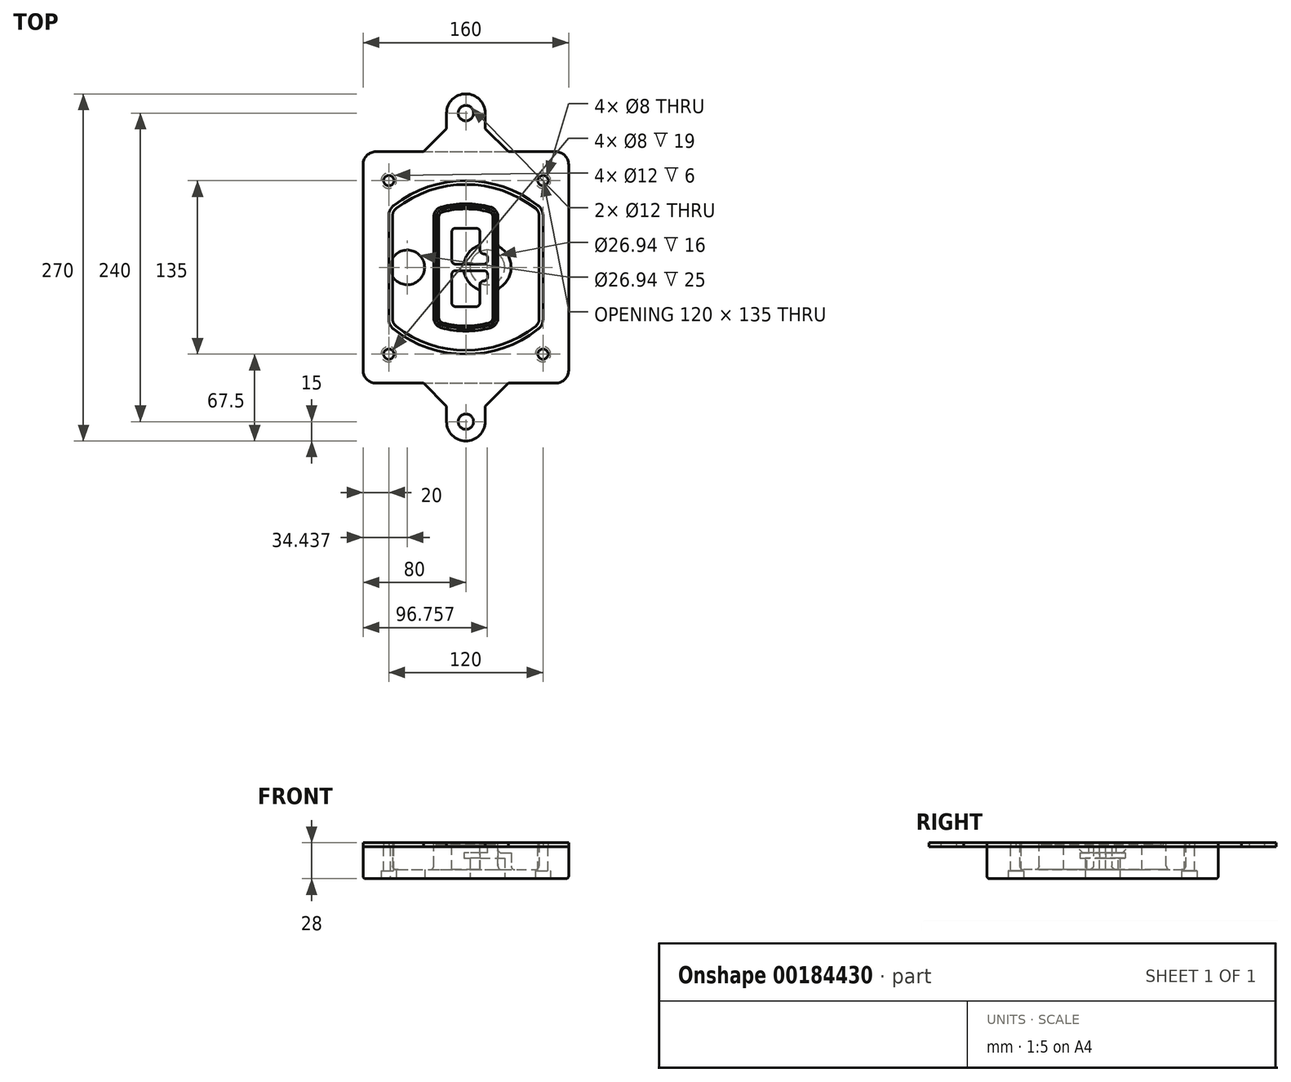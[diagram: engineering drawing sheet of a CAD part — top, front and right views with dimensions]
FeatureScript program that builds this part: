
annotation { "Feature Type Name" : "Feature", "Feature Type Description" : "" }
export const myFeature = defineFeature(function(context is Context, id is Id, definition is map)
    precondition{}
    {
        {
            var Q0;
            Q0=qCreatedBy(makeId("Top.planeOp"),FACE);
            var sketch = newSketch(context, id + "F0", { "sketchPlane" : qUnion([Q0])});
            skPoint(sketch, "E0.rect.middle", {"position": v(0, 0) * mm});
            skLineSegment(sketch, "E1.bottom", {"start": v(-70, -90) * mm, "end": v(70, -90) * mm});
            skLineSegment(sketch, "E1.top", {"start": v(-70, 90) * mm, "end": v(70, 90) * mm});
            skLineSegment(sketch, "E1.left", {"start": v(-80, -80) * mm, "end": v(-80, 80) * mm});
            skLineSegment(sketch, "E1.right", {"start": v(80, -80) * mm, "end": v(80, 80) * mm});
            skLineSegment(sketch, "E2", {"start": v(-80, 90) * mm, "end": v(80, -90) * mm, "construction": true});
            skLineSegment(sketch, "E3", {"start": v(80, 90) * mm, "end": v(-80, -90) * mm, "construction": true});
            skCircle(sketch, "E4", {"center": v(-60, 67.5) * mm, "radius": 4 * mm});
            skCircle(sketch, "E5", {"center": v(60, 67.5) * mm, "radius": 4 * mm});
            skCircle(sketch, "E6", {"center": v(60, -67.5) * mm, "radius": 4 * mm});
            skCircle(sketch, "E7", {"center": v(-60, -67.5) * mm, "radius": 4 * mm});
            skLineSegment(sketch, "E8", {"start": v(-60, 67.5) * mm, "end": v(60, 67.5) * mm, "construction": true});
            skLineSegment(sketch, "E9", {"start": v(60, 67.5) * mm, "end": v(60, -67.5) * mm, "construction": true});
            skLineSegment(sketch, "E10", {"start": v(60, -67.5) * mm, "end": v(-60, -67.5) * mm, "construction": true});
            skLineSegment(sketch, "E11", {"start": v(-60, -67.5) * mm, "end": v(-60, 67.5) * mm, "construction": true});
            skLineSegment(sketch, "E12", {"start": v(-60, 40.3) * mm, "end": v(-60, -40.3) * mm});
            skLineSegment(sketch, "E13", {"start": v(60, 40.3) * mm, "end": v(60, -40.3) * mm});
            skArc(sketch, "E14", {"start": v(56.15, 48.18) * mm, "mid": v(0, 67.5) * mm, "end": v(-56.15, 48.18) * mm});
            skArc(sketch, "E15", {"start": v(-56.15, -48.18) * mm, "mid": v(0, -67.5) * mm, "end": v(56.15, -48.18) * mm});
            skLineSegment(sketch, "E16", {"start": v(-60, 0) * mm, "end": v(60, 0) * mm, "construction": true});
            skPoint(sketch, "E17.visualSharp", {"position": v(-60, -45) * mm});
            skArc(sketch, "E17.filletArc", {"start": v(-60, -40.3) * mm, "mid": v(-58.99, -44.68) * mm, "end": v(-56.15, -48.18) * mm});
            skPoint(sketch, "E18.visualSharp", {"position": v(-60, 45) * mm});
            skArc(sketch, "E18.filletArc", {"start": v(-56.15, 48.18) * mm, "mid": v(-58.99, 44.68) * mm, "end": v(-60, 40.3) * mm});
            skPoint(sketch, "E19.visualSharp", {"position": v(60, 45) * mm});
            skArc(sketch, "E19.filletArc", {"start": v(60, 40.3) * mm, "mid": v(58.99, 44.68) * mm, "end": v(56.15, 48.18) * mm});
            skPoint(sketch, "E20.visualSharp", {"position": v(60, -45) * mm});
            skArc(sketch, "E20.filletArc", {"start": v(56.15, -48.18) * mm, "mid": v(58.99, -44.68) * mm, "end": v(60, -40.3) * mm});
            skPoint(sketch, "E21.visualSharp", {"position": v(-80, 90) * mm});
            skArc(sketch, "E21.filletArc", {"start": v(-70, 90) * mm, "mid": v(-77.07, 87.07) * mm, "end": v(-80, 80) * mm});
            skPoint(sketch, "E22.visualSharp", {"position": v(80, 90) * mm});
            skArc(sketch, "E22.filletArc", {"start": v(80, 80) * mm, "mid": v(77.07, 87.07) * mm, "end": v(70, 90) * mm});
            skPoint(sketch, "E23.visualSharp", {"position": v(80, -90) * mm});
            skArc(sketch, "E23.filletArc", {"start": v(70, -90) * mm, "mid": v(77.07, -87.07) * mm, "end": v(80, -80) * mm});
            skPoint(sketch, "E24.visualSharp", {"position": v(-80, -90) * mm});
            skArc(sketch, "E24.filletArc", {"start": v(-80, -80) * mm, "mid": v(-77.07, -87.07) * mm, "end": v(-70, -90) * mm});
            skArc(sketch, "E25.0", {"start": v(57, 40.3) * mm, "mid": v(56.3, 43.36) * mm, "end": v(54.3, 45.81) * mm});
            skLineSegment(sketch, "E25.1", {"start": v(57, 40.3) * mm, "end": v(57, -40.3) * mm});
            skArc(sketch, "E25.2", {"start": v(54.3, -45.81) * mm, "mid": v(56.3, -43.36) * mm, "end": v(57, -40.3) * mm});
            skArc(sketch, "E25.3", {"start": v(-54.3, -45.81) * mm, "mid": v(0, -64.5) * mm, "end": v(54.3, -45.81) * mm});
            skArc(sketch, "E25.4", {"start": v(-57, -40.3) * mm, "mid": v(-56.3, -43.36) * mm, "end": v(-54.3, -45.81) * mm});
            skArc(sketch, "E25.5", {"start": v(54.3, 45.81) * mm, "mid": v(0, 64.5) * mm, "end": v(-54.3, 45.81) * mm});
            skLineSegment(sketch, "E25.6", {"start": v(-57, 40.3) * mm, "end": v(-57, -40.3) * mm});
            skArc(sketch, "E25.7", {"start": v(-54.3, 45.81) * mm, "mid": v(-56.3, 43.36) * mm, "end": v(-57, 40.3) * mm});
            skArc(sketch, "E26.0", {"start": v(-58.62, 51.33) * mm, "mid": v(-62.58, 46.43) * mm, "end": v(-64, 40.3) * mm});
            skArc(sketch, "E26.1", {"start": v(58.62, 51.33) * mm, "mid": v(0, 71.5) * mm, "end": v(-58.62, 51.33) * mm});
            skArc(sketch, "E26.2", {"start": v(64, 40.3) * mm, "mid": v(62.58, 46.43) * mm, "end": v(58.62, 51.33) * mm});
            skLineSegment(sketch, "E26.3", {"start": v(64, 40.3) * mm, "end": v(64, -40.3) * mm});
            skArc(sketch, "E26.4", {"start": v(58.62, -51.33) * mm, "mid": v(62.58, -46.43) * mm, "end": v(64, -40.3) * mm});
            skLineSegment(sketch, "E26.5", {"start": v(-64, 40.3) * mm, "end": v(-64, -40.3) * mm});
            skArc(sketch, "E26.6", {"start": v(-58.62, -51.33) * mm, "mid": v(0, -71.5) * mm, "end": v(58.62, -51.33) * mm});
            skArc(sketch, "E26.7", {"start": v(-64, -40.3) * mm, "mid": v(-62.58, -46.43) * mm, "end": v(-58.62, -51.33) * mm});
            skSolve(sketch);
        }
        {
            var Q0;
            Q0=makeQuery(id+"F0.imprint","IMPRINT",FACE,{"disambiguationData":[TD([[makeQuery(id+"F0.imprint","IMPRINT",EDGE,{"derivedFrom":sQuery(id+"F0.wireOp",EDGE,"E1.bottom")}),1.0]])]});
            var Q1;
            Q1=makeQuery(id+"F0.imprint","IMPRINT",FACE,{"disambiguationData":[TD([[makeQuery(id+"F0.imprint","IMPRINT",EDGE,{"derivedFrom":sQuery(id+"F0.wireOp",EDGE,"E12")}),1.0]])]});
            var Q2;
            Q2=makeQuery(id+"F0.imprint","IMPRINT",FACE,{"disambiguationData":[TD([[makeQuery(id+"F0.imprint","IMPRINT",EDGE,{"derivedFrom":sQuery(id+"F0.wireOp",EDGE,"E25.0")}),1.0]])]});
            var Q3;
            Q3=makeQuery(id+"F0.imprint","IMPRINT",FACE,{"disambiguationData":[TD([[makeQuery(id+"F0.imprint","IMPRINT",EDGE,{"derivedFrom":sQuery(id+"F0.wireOp",EDGE,"E12")}),-1.0]])]});
            extrude(context, id + "F1", {"entities" : qUnion([Q0, Q1, Q2, Q3]), "oppositeDirection" : true, "depth" : 25 * mm});
        }
        {
            var Q0;
            Q0=makeQuery(id+"F0.imprint","IMPRINT",FACE,{"disambiguationData":[TD([[makeQuery(id+"F0.imprint","IMPRINT",EDGE,{"derivedFrom":sQuery(id+"F0.wireOp",EDGE,"E12")}),1.0]])]});
            extrude(context, id + "F2", {"entities" : qUnion([Q0]), "operationType" : NewBodyOperationType.ADD, "depth" : 3 * mm});
        }
        {
            var Q0;
            Q0=makeQuery(id+"F0.imprint","IMPRINT",FACE,{"disambiguationData":[TD([[makeQuery(id+"F0.imprint","IMPRINT",EDGE,{"derivedFrom":sQuery(id+"F0.wireOp",EDGE,"E25.0")}),1.0]])]});
            extrude(context, id + "F3", {"entities" : qUnion([Q0]), "operationType" : NewBodyOperationType.REMOVE, "oppositeDirection" : true, "depth" : 18 * mm});
        }
        {
            var Q0;
            Q0=makeQuery(id+"F2.opExtrude","CAP_FACE",FACE,{"disambiguationData":[OSD([sQuery(id+"F0.wireOp",EDGE,"E12"),sQuery(id+"F0.wireOp",EDGE,"E13"),sQuery(id+"F0.wireOp",EDGE,"E14"),sQuery(id+"F0.wireOp",EDGE,"E15"),sQuery(id+"F0.wireOp",EDGE,"E17.filletArc"),sQuery(id+"F0.wireOp",EDGE,"E18.filletArc"),sQuery(id+"F0.wireOp",EDGE,"E19.filletArc"),sQuery(id+"F0.wireOp",EDGE,"E20.filletArc"),sQuery(id+"F0.wireOp",EDGE,"E25.0"),sQuery(id+"F0.wireOp",EDGE,"E25.1"),sQuery(id+"F0.wireOp",EDGE,"E25.2"),sQuery(id+"F0.wireOp",EDGE,"E25.3"),sQuery(id+"F0.wireOp",EDGE,"E25.4"),sQuery(id+"F0.wireOp",EDGE,"E25.5"),sQuery(id+"F0.wireOp",EDGE,"E25.6"),sQuery(id+"F0.wireOp",EDGE,"E25.7")])],"isStart":false});
            var sketch = newSketch(context, id + "F4", { "sketchPlane" : qUnion([Q0])});
            skArc(sketch, "E27.0", {"start": v(-19.08, -46.97) * mm, "mid": v(0, -49.5) * mm, "end": v(19.08, -46.97) * mm});
            skArc(sketch, "E28.0", {"start": v(19.08, 46.97) * mm, "mid": v(0, 49.5) * mm, "end": v(-19.08, 46.97) * mm});
            skLineSegment(sketch, "E29", {"start": v(-25, 39.25) * mm, "end": v(-25, -39.25) * mm});
            skLineSegment(sketch, "E30", {"start": v(25, 39.25) * mm, "end": v(25, -39.25) * mm});
            skLineSegment(sketch, "E31", {"start": v(-25, 45.1) * mm, "end": v(25, 45.1) * mm, "construction": true});
            skLineSegment(sketch, "E32", {"start": v(-25, -45.1) * mm, "end": v(25, -45.1) * mm, "construction": true});
            skPoint(sketch, "E33.visualSharp", {"position": v(-25, 45.1) * mm});
            skArc(sketch, "E33.filletArc", {"start": v(-19.08, 46.97) * mm, "mid": v(-23.35, 44.11) * mm, "end": v(-25, 39.25) * mm});
            skPoint(sketch, "E34.visualSharp", {"position": v(25, 45.1) * mm});
            skArc(sketch, "E34.filletArc", {"start": v(25, 39.25) * mm, "mid": v(23.35, 44.11) * mm, "end": v(19.08, 46.97) * mm});
            skPoint(sketch, "E35.visualSharp", {"position": v(25, -45.1) * mm});
            skArc(sketch, "E35.filletArc", {"start": v(19.08, -46.97) * mm, "mid": v(23.35, -44.11) * mm, "end": v(25, -39.25) * mm});
            skPoint(sketch, "E36.visualSharp", {"position": v(-25, -45.1) * mm});
            skArc(sketch, "E36.filletArc", {"start": v(-25, -39.25) * mm, "mid": v(-23.35, -44.11) * mm, "end": v(-19.08, -46.97) * mm});
            skArc(sketch, "E37.0", {"start": v(54.3, 45.81) * mm, "mid": v(0, 64.5) * mm, "end": v(-54.3, 45.81) * mm});
            skArc(sketch, "E37.1", {"start": v(-54.3, 45.81) * mm, "mid": v(-56.3, 43.36) * mm, "end": v(-57, 40.3) * mm});
            skLineSegment(sketch, "E37.2", {"start": v(-57, 40.3) * mm, "end": v(-57, -40.3) * mm});
            skArc(sketch, "E37.3", {"start": v(-57, -40.3) * mm, "mid": v(-56.3, -43.36) * mm, "end": v(-54.3, -45.81) * mm});
            skArc(sketch, "E37.4", {"start": v(-54.3, -45.81) * mm, "mid": v(0, -64.5) * mm, "end": v(54.3, -45.81) * mm});
            skArc(sketch, "E37.5", {"start": v(54.3, -45.81) * mm, "mid": v(56.3, -43.36) * mm, "end": v(57, -40.3) * mm});
            skLineSegment(sketch, "E37.6", {"start": v(57, 40.3) * mm, "end": v(57, -40.3) * mm});
            skArc(sketch, "E37.7", {"start": v(57, 40.3) * mm, "mid": v(56.3, 43.36) * mm, "end": v(54.3, 45.81) * mm});
            skLineSegment(sketch, "E38.0", {"start": v(23, 39.25) * mm, "end": v(23, -39.25) * mm});
            skArc(sketch, "E38.1", {"start": v(18.56, -45.04) * mm, "mid": v(21.76, -42.9) * mm, "end": v(23, -39.25) * mm});
            skArc(sketch, "E38.2", {"start": v(-18.56, -45.04) * mm, "mid": v(0, -47.5) * mm, "end": v(18.56, -45.04) * mm});
            skArc(sketch, "E38.3", {"start": v(-23, -39.25) * mm, "mid": v(-21.76, -42.9) * mm, "end": v(-18.56, -45.04) * mm});
            skLineSegment(sketch, "E38.4", {"start": v(-23, 39.25) * mm, "end": v(-23, -39.25) * mm});
            skArc(sketch, "E38.5", {"start": v(23, 39.25) * mm, "mid": v(21.76, 42.9) * mm, "end": v(18.56, 45.04) * mm});
            skArc(sketch, "E38.6", {"start": v(-18.56, 45.04) * mm, "mid": v(-21.76, 42.9) * mm, "end": v(-23, 39.25) * mm});
            skArc(sketch, "E38.7", {"start": v(18.56, 45.04) * mm, "mid": v(0, 47.5) * mm, "end": v(-18.56, 45.04) * mm});
            skArc(sketch, "E39.0", {"start": v(21, 39.25) * mm, "mid": v(20.18, 41.68) * mm, "end": v(18.04, 43.1) * mm});
            skLineSegment(sketch, "E39.1", {"start": v(21, 39.25) * mm, "end": v(21, -39.25) * mm});
            skArc(sketch, "E39.2", {"start": v(18.04, -43.1) * mm, "mid": v(20.18, -41.68) * mm, "end": v(21, -39.25) * mm});
            skArc(sketch, "E39.3", {"start": v(-18.04, -43.1) * mm, "mid": v(0, -45.5) * mm, "end": v(18.04, -43.1) * mm});
            skArc(sketch, "E39.4", {"start": v(-21, -39.25) * mm, "mid": v(-20.18, -41.68) * mm, "end": v(-18.04, -43.1) * mm});
            skArc(sketch, "E39.5", {"start": v(18.04, 43.1) * mm, "mid": v(0, 45.5) * mm, "end": v(-18.04, 43.1) * mm});
            skLineSegment(sketch, "E39.6", {"start": v(-21, 39.25) * mm, "end": v(-21, -39.25) * mm});
            skArc(sketch, "E39.7", {"start": v(-18.04, 43.1) * mm, "mid": v(-20.18, 41.68) * mm, "end": v(-21, 39.25) * mm});
            skLineSegment(sketch, "E40", {"start": v(-25, 0) * mm, "end": v(25, 0) * mm, "construction": true});
            skLineSegment(sketch, "E41", {"start": v(-11, 5.5) * mm, "end": v(-11, 27.5) * mm});
            skLineSegment(sketch, "E42", {"start": v(-8, 30.5) * mm, "end": v(8, 30.5) * mm});
            skLineSegment(sketch, "E43", {"start": v(11, 27.5) * mm, "end": v(11, 13.5) * mm});
            skLineSegment(sketch, "E44", {"start": v(14, 10.5) * mm, "end": v(14, 10.5) * mm});
            skLineSegment(sketch, "E45", {"start": v(17, 7.5) * mm, "end": v(17, 5.5) * mm});
            skLineSegment(sketch, "E46", {"start": v(14, 2.5) * mm, "end": v(-8, 2.5) * mm});
            skPoint(sketch, "E47.visualSharp", {"position": v(-11, 30.5) * mm});
            skArc(sketch, "E47.filletArc", {"start": v(-8, 30.5) * mm, "mid": v(-10.12, 29.62) * mm, "end": v(-11, 27.5) * mm});
            skPoint(sketch, "E48.visualSharp", {"position": v(11, 30.5) * mm});
            skArc(sketch, "E48.filletArc", {"start": v(11, 27.5) * mm, "mid": v(10.12, 29.62) * mm, "end": v(8, 30.5) * mm});
            skPoint(sketch, "E49.visualSharp", {"position": v(11, 10.5) * mm});
            skArc(sketch, "E49.filletArc", {"start": v(11, 13.5) * mm, "mid": v(11.88, 11.38) * mm, "end": v(14, 10.5) * mm});
            skPoint(sketch, "E50.visualSharp", {"position": v(17, 10.5) * mm});
            skArc(sketch, "E50.filletArc", {"start": v(17, 7.5) * mm, "mid": v(16.12, 9.62) * mm, "end": v(14, 10.5) * mm});
            skPoint(sketch, "E51.visualSharp", {"position": v(17, 2.5) * mm});
            skArc(sketch, "E51.filletArc", {"start": v(14, 2.5) * mm, "mid": v(16.12, 3.38) * mm, "end": v(17, 5.5) * mm});
            skPoint(sketch, "E52.visualSharp", {"position": v(-11, 2.5) * mm});
            skArc(sketch, "E52.filletArc", {"start": v(-11, 5.5) * mm, "mid": v(-10.12, 3.38) * mm, "end": v(-8, 2.5) * mm});
            skLineSegment(sketch, "E53.0.MirrorCS", {"start": v(14, -2.5) * mm, "end": v(-8, -2.5) * mm});
            skArc(sketch, "E54.0.MirrorCS", {"start": v(-11, -5.5) * mm, "mid": v(-10.12, -3.38) * mm, "end": v(-8, -2.5) * mm});
            skLineSegment(sketch, "E55.0.MirrorCS", {"start": v(-11, -5.5) * mm, "end": v(-11, -27.5) * mm});
            skArc(sketch, "E56.0.MirrorCS", {"start": v(-8, -30.5) * mm, "mid": v(-10.12, -29.62) * mm, "end": v(-11, -27.5) * mm});
            skLineSegment(sketch, "E57.0.MirrorCS", {"start": v(-8, -30.5) * mm, "end": v(8, -30.5) * mm});
            skArc(sketch, "E58.0.MirrorCS", {"start": v(11, -27.5) * mm, "mid": v(10.12, -29.62) * mm, "end": v(8, -30.5) * mm});
            skLineSegment(sketch, "E59.0.MirrorCS", {"start": v(11, -27.5) * mm, "end": v(11, -13.5) * mm});
            skArc(sketch, "E60.0.MirrorCS", {"start": v(11, -13.5) * mm, "mid": v(11.88, -11.38) * mm, "end": v(14, -10.5) * mm});
            skArc(sketch, "E61.0.MirrorCS", {"start": v(17, -7.5) * mm, "mid": v(16.12, -9.62) * mm, "end": v(14, -10.5) * mm});
            skLineSegment(sketch, "E62.0.MirrorCS", {"start": v(17, -7.5) * mm, "end": v(17, -5.5) * mm});
            skArc(sketch, "E63.0.MirrorCS", {"start": v(14, -2.5) * mm, "mid": v(16.12, -3.38) * mm, "end": v(17, -5.5) * mm});
            skSolve(sketch);
        }
        {
            var Q0;
            Q0=makeQuery(id+"F4.imprint","IMPRINT",FACE,{"disambiguationData":[TD([[makeQuery(id+"F4.imprint","IMPRINT",EDGE,{"derivedFrom":sQuery(id+"F4.wireOp",EDGE,"E27.0")}),1.0]])]});
            var Q1;
            Q1=makeQuery(id+"F4.imprint","IMPRINT",FACE,{"disambiguationData":[TD([[makeQuery(id+"F4.imprint","IMPRINT",EDGE,{"derivedFrom":sQuery(id+"F4.wireOp",EDGE,"E38.0")}),-1.0]])]});
            var Q2;
            Q2=makeQuery(id+"F4.imprint","IMPRINT",FACE,{"disambiguationData":[TD([[makeQuery(id+"F4.imprint","IMPRINT",EDGE,{"derivedFrom":sQuery(id+"F4.wireOp",EDGE,"E39.0")}),1.0]])]});
            extrude(context, id + "F5", {"entities" : qUnion([Q0, Q1, Q2]), "operationType" : NewBodyOperationType.ADD, "endBound" : BoundingType.UP_TO_NEXT, "oppositeDirection" : true, "depth" : 25 * mm});
        }
        {
            var Q0;
            Q0=makeQuery(id+"F4.imprint","IMPRINT",FACE,{"disambiguationData":[TD([[makeQuery(id+"F4.imprint","IMPRINT",EDGE,{"derivedFrom":sQuery(id+"F4.wireOp",EDGE,"E38.0")}),-1.0]])]});
            extrude(context, id + "F6", {"entities" : qUnion([Q0]), "operationType" : NewBodyOperationType.REMOVE, "oppositeDirection" : true, "depth" : 2 * mm});
        }
        {
            var Q0;
            Q0=makeQuery(id+"F1.opExtrude","CAP_FACE",FACE,{"disambiguationData":[OSD([sQuery(id+"F0.wireOp",EDGE,"E1.bottom"),sQuery(id+"F0.wireOp",EDGE,"E1.top"),sQuery(id+"F0.wireOp",EDGE,"E1.left"),sQuery(id+"F0.wireOp",EDGE,"E1.right"),sQuery(id+"F0.wireOp",EDGE,"E4"),sQuery(id+"F0.wireOp",EDGE,"E5"),sQuery(id+"F0.wireOp",EDGE,"E6"),sQuery(id+"F0.wireOp",EDGE,"E7"),sQuery(id+"F0.wireOp",EDGE,"E21.filletArc"),sQuery(id+"F0.wireOp",EDGE,"E22.filletArc"),sQuery(id+"F0.wireOp",EDGE,"E23.filletArc"),sQuery(id+"F0.wireOp",EDGE,"E24.filletArc")])],"isStart":false});
            var sketch = newSketch(context, id + "F7", { "sketchPlane" : qUnion([Q0])});
            skCircle(sketch, "E64", {"center": v(16.76, 0) * mm, "radius": 13.47 * mm});
            skCircle(sketch, "E65", {"center": v(-45.56, 0) * mm, "radius": 13.47 * mm});
            skLineSegment(sketch, "E66", {"start": v(80, 0) * mm, "end": v(-80, 0) * mm});
            skCircle(sketch, "E67", {"center": v(16.76, 0) * mm, "radius": 18.47 * mm});
            skCircle(sketch, "E68", {"center": v(60, -67.5) * mm, "radius": 6 * mm});
            skCircle(sketch, "E69", {"center": v(-60, -67.5) * mm, "radius": 6 * mm});
            skCircle(sketch, "E70", {"center": v(-60, 67.5) * mm, "radius": 6 * mm});
            skCircle(sketch, "E71", {"center": v(60, 67.5) * mm, "radius": 6 * mm});
            skSolve(sketch);
        }
        {
            var Q0;
            {var subQ1=sQuery(id+"F7.wireOp",EDGE,"E66");var subQ4=sQuery(id+"F7.wireOp",EDGE,"E64");var subQ6=makeQuery(id+"F7.imprint","INTERSECT",VERTEX,{"disambiguationData":[OD(0.0)],"derivedFrom":[subQ4,subQ1]});Q0=makeQuery(id+"F7.imprint","IMPRINT",FACE,{"disambiguationData":[TD([[makeQuery(id+"F7.imprint","IMPRINT",EDGE,{"disambiguationData":[TD([[subQ6,-1.0]])],"derivedFrom":subQ4}),-1.0]])]});}
            var Q1;
            {var subQ0=sQuery(id+"F7.wireOp",EDGE,"E66");var subQ1=sQuery(id+"F7.wireOp",EDGE,"E64");var subQ3=makeQuery(id+"F7.imprint","INTERSECT",VERTEX,{"disambiguationData":[OD(0.0)],"derivedFrom":[subQ1,subQ0]});Q1=makeQuery(id+"F7.imprint","IMPRINT",FACE,{"disambiguationData":[TD([[makeQuery(id+"F7.imprint","IMPRINT",EDGE,{"disambiguationData":[TD([[subQ3,-1.0]])],"derivedFrom":subQ1}),1.0]])]});}
            var Q2;
            {var subQ0=sQuery(id+"F7.wireOp",EDGE,"E66");var subQ1=sQuery(id+"F7.wireOp",EDGE,"E64");var subQ3=makeQuery(id+"F7.imprint","INTERSECT",VERTEX,{"disambiguationData":[OD(0.0)],"derivedFrom":[subQ1,subQ0]});Q2=makeQuery(id+"F7.imprint","IMPRINT",FACE,{"disambiguationData":[TD([[makeQuery(id+"F7.imprint","IMPRINT",EDGE,{"disambiguationData":[TD([[subQ3,1.0]])],"derivedFrom":subQ1}),1.0]])]});}
            var Q3;
            {var subQ1=sQuery(id+"F7.wireOp",EDGE,"E66");var subQ4=sQuery(id+"F7.wireOp",EDGE,"E64");var subQ6=makeQuery(id+"F7.imprint","INTERSECT",VERTEX,{"disambiguationData":[OD(0.0)],"derivedFrom":[subQ4,subQ1]});Q3=makeQuery(id+"F7.imprint","IMPRINT",FACE,{"disambiguationData":[TD([[makeQuery(id+"F7.imprint","IMPRINT",EDGE,{"disambiguationData":[TD([[subQ6,1.0]])],"derivedFrom":subQ4}),-1.0]])]});}
            extrude(context, id + "F8", {"entities" : qUnion([Q0, Q1, Q2, Q3]), "operationType" : NewBodyOperationType.ADD, "oppositeDirection" : true, "depth" : 20 * mm});
        }
        {
            var Q0;
            {var subQ0=sQuery(id+"F7.wireOp",EDGE,"E66");var subQ1=sQuery(id+"F7.wireOp",EDGE,"E64");var subQ3=makeQuery(id+"F7.imprint","INTERSECT",VERTEX,{"disambiguationData":[OD(0.0)],"derivedFrom":[subQ1,subQ0]});Q0=makeQuery(id+"F7.imprint","IMPRINT",FACE,{"disambiguationData":[TD([[makeQuery(id+"F7.imprint","IMPRINT",EDGE,{"disambiguationData":[TD([[subQ3,-1.0]])],"derivedFrom":subQ1}),1.0]])]});}
            var Q1;
            {var subQ0=sQuery(id+"F7.wireOp",EDGE,"E66");var subQ1=sQuery(id+"F7.wireOp",EDGE,"E64");var subQ3=makeQuery(id+"F7.imprint","INTERSECT",VERTEX,{"disambiguationData":[OD(0.0)],"derivedFrom":[subQ1,subQ0]});Q1=makeQuery(id+"F7.imprint","IMPRINT",FACE,{"disambiguationData":[TD([[makeQuery(id+"F7.imprint","IMPRINT",EDGE,{"disambiguationData":[TD([[subQ3,1.0]])],"derivedFrom":subQ1}),1.0]])]});}
            extrude(context, id + "F9", {"entities" : qUnion([Q0, Q1]), "operationType" : NewBodyOperationType.REMOVE, "oppositeDirection" : true, "depth" : 16 * mm});
        }
        {
            var Q0;
            {var subQ0=sQuery(id+"F7.wireOp",EDGE,"E66");var subQ1=sQuery(id+"F7.wireOp",EDGE,"E65");var subQ3=makeQuery(id+"F7.imprint","INTERSECT",VERTEX,{"disambiguationData":[OD(0.0)],"derivedFrom":[subQ1,subQ0]});Q0=makeQuery(id+"F7.imprint","IMPRINT",FACE,{"disambiguationData":[TD([[makeQuery(id+"F7.imprint","IMPRINT",EDGE,{"disambiguationData":[TD([[subQ3,-1.0]])],"derivedFrom":subQ1}),1.0]])]});}
            var Q1;
            {var subQ0=sQuery(id+"F7.wireOp",EDGE,"E66");var subQ1=sQuery(id+"F7.wireOp",EDGE,"E65");var subQ3=makeQuery(id+"F7.imprint","INTERSECT",VERTEX,{"disambiguationData":[OD(0.0)],"derivedFrom":[subQ1,subQ0]});Q1=makeQuery(id+"F7.imprint","IMPRINT",FACE,{"disambiguationData":[TD([[makeQuery(id+"F7.imprint","IMPRINT",EDGE,{"disambiguationData":[TD([[subQ3,1.0]])],"derivedFrom":subQ1}),1.0]])]});}
            extrude(context, id + "F10", {"entities" : qUnion([Q0, Q1]), "operationType" : NewBodyOperationType.REMOVE, "oppositeDirection" : true, "depth" : 25 * mm});
        }
        {
            var Q0;
            Q0=makeQuery(id+"F7.imprint","IMPRINT",FACE,{"disambiguationData":[TD([[makeQuery(id+"F7.imprint","IMPRINT",EDGE,{"derivedFrom":sQuery(id+"F7.wireOp",EDGE,"E68")}),1.0]])]});
            var Q1;
            Q1=makeQuery(id+"F7.imprint","IMPRINT",FACE,{"disambiguationData":[TD([[makeQuery(id+"F7.imprint","IMPRINT",EDGE,{"derivedFrom":makeQuery(id+"F1.opExtrude","CAP_EDGE",EDGE,{"disambiguationData":[OSD([sQuery(id+"F0.wireOp",EDGE,"E5")])],"isStart":false})}),-1.0]])]});
            var Q2;
            Q2=makeQuery(id+"F7.imprint","IMPRINT",FACE,{"disambiguationData":[TD([[makeQuery(id+"F7.imprint","IMPRINT",EDGE,{"derivedFrom":sQuery(id+"F7.wireOp",EDGE,"E69")}),1.0]])]});
            var Q3;
            Q3=makeQuery(id+"F7.imprint","IMPRINT",FACE,{"disambiguationData":[TD([[makeQuery(id+"F7.imprint","IMPRINT",EDGE,{"derivedFrom":makeQuery(id+"F1.opExtrude","CAP_EDGE",EDGE,{"disambiguationData":[OSD([sQuery(id+"F0.wireOp",EDGE,"E4")])],"isStart":false})}),-1.0]])]});
            var Q4;
            Q4=makeQuery(id+"F7.imprint","IMPRINT",FACE,{"disambiguationData":[TD([[makeQuery(id+"F7.imprint","IMPRINT",EDGE,{"derivedFrom":sQuery(id+"F7.wireOp",EDGE,"E70")}),1.0]])]});
            var Q5;
            Q5=makeQuery(id+"F7.imprint","IMPRINT",FACE,{"disambiguationData":[TD([[makeQuery(id+"F7.imprint","IMPRINT",EDGE,{"derivedFrom":makeQuery(id+"F1.opExtrude","CAP_EDGE",EDGE,{"disambiguationData":[OSD([sQuery(id+"F0.wireOp",EDGE,"E7")])],"isStart":false})}),-1.0]])]});
            var Q6;
            Q6=makeQuery(id+"F7.imprint","IMPRINT",FACE,{"disambiguationData":[TD([[makeQuery(id+"F7.imprint","IMPRINT",EDGE,{"derivedFrom":sQuery(id+"F7.wireOp",EDGE,"E71")}),1.0]])]});
            var Q7;
            Q7=makeQuery(id+"F7.imprint","IMPRINT",FACE,{"disambiguationData":[TD([[makeQuery(id+"F7.imprint","IMPRINT",EDGE,{"derivedFrom":makeQuery(id+"F1.opExtrude","CAP_EDGE",EDGE,{"disambiguationData":[OSD([sQuery(id+"F0.wireOp",EDGE,"E6")])],"isStart":false})}),-1.0]])]});
            extrude(context, id + "F11", {"entities" : qUnion([Q0, Q1, Q2, Q3, Q4, Q5, Q6, Q7]), "operationType" : NewBodyOperationType.REMOVE, "oppositeDirection" : true, "depth" : 6 * mm});
        }
        {
            var Q0;
            Q0=makeQuery(id+"F9.boolean.opBoolean","COPY",FACE,{"derivedFrom":makeQuery(id+"F9.opExtrude","CAP_FACE",FACE,{"disambiguationData":[OSD([sQuery(id+"F7.wireOp",EDGE,"E64")])],"isStart":false})});
            var sketch = newSketch(context, id + "F12", { "sketchPlane" : qUnion([Q0])});
            skArc(sketch, "E72.0", {"start": v(11, 17.55) * mm, "mid": v(2.57, 11.82) * mm, "end": v(-1.54, 2.5) * mm});
            skArc(sketch, "E72.1", {"start": v(-1.54, -2.5) * mm, "mid": v(2.57, -11.82) * mm, "end": v(11, -17.55) * mm});
            skLineSegment(sketch, "E73", {"start": v(-1.54, -2.5) * mm, "end": v(14, -2.5) * mm});
            skLineSegment(sketch, "E74.0", {"start": v(14, 2.5) * mm, "end": v(-1.54, 2.5) * mm});
            skArc(sketch, "E74.1", {"start": v(14, 2.5) * mm, "mid": v(16.12, 3.38) * mm, "end": v(17, 5.5) * mm});
            skLineSegment(sketch, "E74.2", {"start": v(17, 7.5) * mm, "end": v(17, 5.5) * mm});
            skArc(sketch, "E74.3", {"start": v(17, 7.5) * mm, "mid": v(16.12, 9.62) * mm, "end": v(14, 10.5) * mm});
            skArc(sketch, "E74.4", {"start": v(11, 13.5) * mm, "mid": v(11.88, 11.38) * mm, "end": v(14, 10.5) * mm});
            skLineSegment(sketch, "E74.5", {"start": v(11, 17.55) * mm, "end": v(11, 13.5) * mm});
            skLineSegment(sketch, "E74.7", {"start": v(14, -2.5) * mm, "end": v(-1.54, -2.5) * mm});
            skArc(sketch, "E74.8", {"start": v(14, -2.5) * mm, "mid": v(16.12, -3.38) * mm, "end": v(17, -5.5) * mm});
            skLineSegment(sketch, "E74.9", {"start": v(17, -7.5) * mm, "end": v(17, -5.5) * mm});
            skArc(sketch, "E74.10", {"start": v(17, -7.5) * mm, "mid": v(16.12, -9.62) * mm, "end": v(14, -10.5) * mm});
            skArc(sketch, "E74.11", {"start": v(11, -13.5) * mm, "mid": v(11.88, -11.38) * mm, "end": v(14, -10.5) * mm});
            skLineSegment(sketch, "E74.12", {"start": v(11, -17.55) * mm, "end": v(11, -13.5) * mm});
            skPoint(sketch, "E75.orphan", {"position": v(11, -27.5) * mm});
            skPoint(sketch, "E76.orphan", {"position": v(-8, -2.5) * mm});
            skPoint(sketch, "E77.orphan", {"position": v(-8, 2.5) * mm});
            skPoint(sketch, "E78.orphan", {"position": v(11, 27.5) * mm});
            skSolve(sketch);
        }
        {
            var Q0;
            {var subQ7=sQuery(id+"F12.wireOp",EDGE,"E72.0");var subQ14=sQuery(id+"F12.wireOp",EDGE,"E72.1");var subQ16=sQuery(id+"F12.wireOp",EDGE,"E74.1");var subQ18=sQuery(id+"F12.wireOp",EDGE,"E74.8");Q0=qUnion([makeQuery(id+"F12.imprint","IMPRINT",FACE,{"disambiguationData":[TD([[makeQuery(id+"F12.imprint","IMPRINT",EDGE,{"derivedFrom":subQ7}),1.0]])]}),makeQuery(id+"F12.imprint","IMPRINT",FACE,{"disambiguationData":[TD([[makeQuery(id+"F12.imprint","IMPRINT",EDGE,{"derivedFrom":subQ14}),1.0]])]}),makeQuery(id+"F12.imprint","IMPRINT",FACE,{"disambiguationData":[TD([[makeQuery(id+"F12.imprint","IMPRINT",EDGE,{"derivedFrom":subQ16}),1.0]])]}),makeQuery(id+"F12.imprint","IMPRINT",FACE,{"disambiguationData":[TD([[makeQuery(id+"F12.imprint","IMPRINT",EDGE,{"derivedFrom":subQ18}),-1.0]])]})]);}
            var Q1;
            Q1=makeQuery(id+"F5.boolean.opBoolean","SPLIT",FACE,{"disambiguationData":[TD([makeQuery(id+"F5.opExtrude","SWEPT_FACE",FACE,{"disambiguationData":[OSD([sQuery(id+"F4.wireOp",EDGE,"E41")])]})])],"derivedFrom":makeQuery(id+"F3.boolean.opBoolean","COPY",FACE,{"derivedFrom":makeQuery(id+"F3.opExtrude","CAP_FACE",FACE,{"disambiguationData":[OSD([sQuery(id+"F0.wireOp",EDGE,"E25.0"),sQuery(id+"F0.wireOp",EDGE,"E25.1"),sQuery(id+"F0.wireOp",EDGE,"E25.2"),sQuery(id+"F0.wireOp",EDGE,"E25.3"),sQuery(id+"F0.wireOp",EDGE,"E25.4"),sQuery(id+"F0.wireOp",EDGE,"E25.5"),sQuery(id+"F0.wireOp",EDGE,"E25.6"),sQuery(id+"F0.wireOp",EDGE,"E25.7")])],"isStart":false})})});
            extrude(context, id + "F13", {"entities" : qUnion([Q0]), "operationType" : NewBodyOperationType.REMOVE, "endBound" : BoundingType.UP_TO_SURFACE, "endBoundEntityFace" : qUnion([Q1]), "depth" : 25 * mm});
        }
        {
            var Q0;
            Q0=makeQuery(id+"F3.boolean.opBoolean","COPY",EDGE,{"derivedFrom":makeQuery(id+"F3.opExtrude","CAP_EDGE",EDGE,{"disambiguationData":[OSD([sQuery(id+"F0.wireOp",EDGE,"E25.6")])],"isStart":false})});
            var Q1;
            Q1=makeQuery(id+"F8.boolean.opBoolean","INTERSECT",EDGE,{"derivedFrom":[makeQuery(id+"F5.opExtrude","SWEPT_FACE",FACE,{"disambiguationData":[OSD([sQuery(id+"F4.wireOp",EDGE,"E30")])]}),makeQuery(id+"F8.opExtrude","CAP_FACE",FACE,{"disambiguationData":[OSD([sQuery(id+"F7.wireOp",EDGE,"E67")])],"isStart":false})]});
            var Q2;
            Q2=makeQuery(id+"F8.boolean.opBoolean","INTERSECT",EDGE,{"disambiguationData":[OD(1.0)],"derivedFrom":[makeQuery(id+"F5.opExtrude","SWEPT_FACE",FACE,{"disambiguationData":[OSD([sQuery(id+"F4.wireOp",EDGE,"E30")])]}),makeQuery(id+"F8.opExtrude","SWEPT_FACE",FACE,{"disambiguationData":[OSD([sQuery(id+"F7.wireOp",EDGE,"E67")])]})]});
            var Q3;
            {var subQ0=sQuery(id+"F4.wireOp",EDGE,"E30");Q3=makeQuery(id+"F8.boolean.opBoolean","SPLIT",EDGE,{"disambiguationData":[TD([makeQuery(id+"F5.opExtrude","SWEPT_FACE",FACE,{"disambiguationData":[OSD([sQuery(id+"F4.wireOp",EDGE,"E35.filletArc")])]})])],"derivedFrom":makeQuery(id+"F5.opExtrude","CAP_EDGE",EDGE,{"disambiguationData":[OSD([subQ0])],"isStart":false})});}
            var Q4;
            {var subQ0=sQuery(id+"F0.wireOp",EDGE,"E25.7");var subQ1=sQuery(id+"F0.wireOp",EDGE,"E25.1");var subQ2=sQuery(id+"F0.wireOp",EDGE,"E25.6");var subQ3=sQuery(id+"F0.wireOp",EDGE,"E25.5");var subQ4=sQuery(id+"F0.wireOp",EDGE,"E25.4");var subQ5=sQuery(id+"F0.wireOp",EDGE,"E25.0");var subQ6=sQuery(id+"F0.wireOp",EDGE,"E25.2");var subQ7=sQuery(id+"F0.wireOp",EDGE,"E25.3");Q4=makeQuery(id+"F8.boolean.opBoolean","INTERSECT",EDGE,{"derivedFrom":[makeQuery(id+"F5.boolean.opBoolean","SPLIT",FACE,{"disambiguationData":[TD([makeQuery(id+"F2.opExtrude","SWEPT_FACE",FACE,{"disambiguationData":[OSD([subQ5])]})])],"derivedFrom":makeQuery(id+"F3.boolean.opBoolean","COPY",FACE,{"derivedFrom":makeQuery(id+"F3.opExtrude","CAP_FACE",FACE,{"disambiguationData":[OSD([subQ5,subQ1,subQ6,subQ7,subQ4,subQ3,subQ2,subQ0])],"isStart":false})})}),makeQuery(id+"F8.opExtrude","SWEPT_FACE",FACE,{"disambiguationData":[OSD([sQuery(id+"F7.wireOp",EDGE,"E67")])]})]});}
            var Q5;
            Q5=makeQuery(id+"F8.boolean.opBoolean","INTERSECT",EDGE,{"disambiguationData":[OD(0.0)],"derivedFrom":[makeQuery(id+"F5.opExtrude","SWEPT_FACE",FACE,{"disambiguationData":[OSD([sQuery(id+"F4.wireOp",EDGE,"E30")])]}),makeQuery(id+"F8.opExtrude","SWEPT_FACE",FACE,{"disambiguationData":[OSD([sQuery(id+"F7.wireOp",EDGE,"E67")])]})]});
            fillet(context, id + "F14", {"entities" : qUnion([Q0, Q1, Q2, Q3, Q4, Q5]), "radius" : 3 * mm, "tangentPropagation" : true, "allowEdgeOverflow" : false});
        }
        {
            var Q0;
            Q0=makeQuery(id+"F1.opExtrude","CAP_EDGE",EDGE,{"disambiguationData":[OSD([sQuery(id+"F0.wireOp",EDGE,"E1.bottom")])],"isStart":false});
            fillet(context, id + "F15", {"entities" : qUnion([Q0]), "radius" : 2 * mm, "tangentPropagation" : true, "allowEdgeOverflow" : false});
        }
        {
            var Q0;
            {var subQ0=sQuery(id+"F0.wireOp",EDGE,"E22.filletArc");var subQ1=sQuery(id+"F0.wireOp",EDGE,"E7");var subQ2=sQuery(id+"F0.wireOp",EDGE,"E6");var subQ3=sQuery(id+"F0.wireOp",EDGE,"E5");var subQ4=sQuery(id+"F0.wireOp",EDGE,"E4");var subQ5=sQuery(id+"F0.wireOp",EDGE,"E1.bottom");var subQ6=sQuery(id+"F0.wireOp",EDGE,"E21.filletArc");var subQ7=sQuery(id+"F0.wireOp",EDGE,"E1.top");var subQ8=sQuery(id+"F0.wireOp",EDGE,"E1.left");var subQ9=sQuery(id+"F0.wireOp",EDGE,"E1.right");var subQ10=sQuery(id+"F0.wireOp",EDGE,"E23.filletArc");var subQ11=sQuery(id+"F0.wireOp",EDGE,"E24.filletArc");Q0=makeQuery(id+"F2.boolean.opBoolean","SPLIT",FACE,{"disambiguationData":[TD([makeQuery(id+"F1.opExtrude","SWEPT_FACE",FACE,{"disambiguationData":[OSD([subQ5])]})])],"derivedFrom":makeQuery(id+"F1.opExtrude","CAP_FACE",FACE,{"disambiguationData":[OSD([subQ5,subQ7,subQ8,subQ9,subQ4,subQ3,subQ2,subQ1,subQ6,subQ0,subQ10,subQ11])],"isStart":true})});}
            var sketch = newSketch(context, id + "F16", { "sketchPlane" : qUnion([Q0])});
            skLineSegment(sketch, "E79", {"start": v(0, 90) * mm, "end": v(0, 120) * mm, "construction": true});
            skCircle(sketch, "E80", {"center": v(0, 120) * mm, "radius": 6 * mm});
            skLineSegment(sketch, "E81", {"start": v(15, 120) * mm, "end": v(15, 108) * mm});
            skLineSegment(sketch, "E82", {"start": v(15, 108) * mm, "end": v(33, 90) * mm});
            skArc(sketch, "E83", {"start": v(15, 120) * mm, "mid": v(0, 135) * mm, "end": v(-15, 120) * mm});
            skLineSegment(sketch, "E84", {"start": v(-15, 120) * mm, "end": v(-15, 108) * mm});
            skLineSegment(sketch, "E85", {"start": v(-15, 108) * mm, "end": v(-33, 90) * mm});
            skLineSegment(sketch, "E86", {"start": v(-80, 0) * mm, "end": v(80, 0) * mm, "construction": true});
            skLineSegment(sketch, "E87.MirrorCS", {"start": v(15, -108) * mm, "end": v(33, -90) * mm});
            skLineSegment(sketch, "E88.MirrorCS", {"start": v(15, -120) * mm, "end": v(15, -108) * mm});
            skArc(sketch, "E89.MirrorCS", {"start": v(15, -120) * mm, "mid": v(0, -135) * mm, "end": v(-15, -120) * mm});
            skCircle(sketch, "E90.MirrorC", {"center": v(0, -120) * mm, "radius": 6 * mm});
            skLineSegment(sketch, "E91.MirrorCS", {"start": v(0, -90) * mm, "end": v(0, -120) * mm, "construction": true});
            skLineSegment(sketch, "E92.MirrorCS", {"start": v(-15, -120) * mm, "end": v(-15, -108) * mm});
            skLineSegment(sketch, "E93.MirrorCS", {"start": v(-15, -108) * mm, "end": v(-33, -90) * mm});
            skSolve(sketch);
        }
        {
            var Q0;
            Q0=makeQuery(id+"F16.imprint","IMPRINT",FACE,{"disambiguationData":[TD([[makeQuery(id+"F16.imprint","IMPRINT",EDGE,{"derivedFrom":sQuery(id+"F16.wireOp",EDGE,"E80")}),-1.0]])]});
            var Q1;
            Q1=makeQuery(id+"F16.imprint","IMPRINT",FACE,{"disambiguationData":[TD([[makeQuery(id+"F16.imprint","IMPRINT",EDGE,{"derivedFrom":makeQuery(id+"F1.opExtrude","CAP_EDGE",EDGE,{"disambiguationData":[OSD([sQuery(id+"F0.wireOp",EDGE,"E1.left")])],"isStart":true})}),-1.0]])]});
            var Q2;
            {var subQ0=sQuery(id+"F16.wireOp",EDGE,"E87.MirrorCS");Q2=makeQuery(id+"F16.imprint","IMPRINT",FACE,{"disambiguationData":[TD([[makeQuery(id+"F16.imprint","IMPRINT",EDGE,{"derivedFrom":subQ0}),1.0]])]});}
            var Q3;
            Q3=makeQuery(id+"F2.opExtrude","CAP_FACE",FACE,{"disambiguationData":[OSD([sQuery(id+"F0.wireOp",EDGE,"E12"),sQuery(id+"F0.wireOp",EDGE,"E13"),sQuery(id+"F0.wireOp",EDGE,"E14"),sQuery(id+"F0.wireOp",EDGE,"E15"),sQuery(id+"F0.wireOp",EDGE,"E17.filletArc"),sQuery(id+"F0.wireOp",EDGE,"E18.filletArc"),sQuery(id+"F0.wireOp",EDGE,"E19.filletArc"),sQuery(id+"F0.wireOp",EDGE,"E20.filletArc"),sQuery(id+"F0.wireOp",EDGE,"E25.0"),sQuery(id+"F0.wireOp",EDGE,"E25.1"),sQuery(id+"F0.wireOp",EDGE,"E25.2"),sQuery(id+"F0.wireOp",EDGE,"E25.3"),sQuery(id+"F0.wireOp",EDGE,"E25.4"),sQuery(id+"F0.wireOp",EDGE,"E25.5"),sQuery(id+"F0.wireOp",EDGE,"E25.6"),sQuery(id+"F0.wireOp",EDGE,"E25.7")])],"isStart":false});
            extrude(context, id + "F17", {"entities" : qUnion([Q0, Q1, Q2]), "endBound" : BoundingType.UP_TO_SURFACE, "endBoundEntityFace" : qUnion([Q3]), "depth" : 25 * mm});
        }
    });
